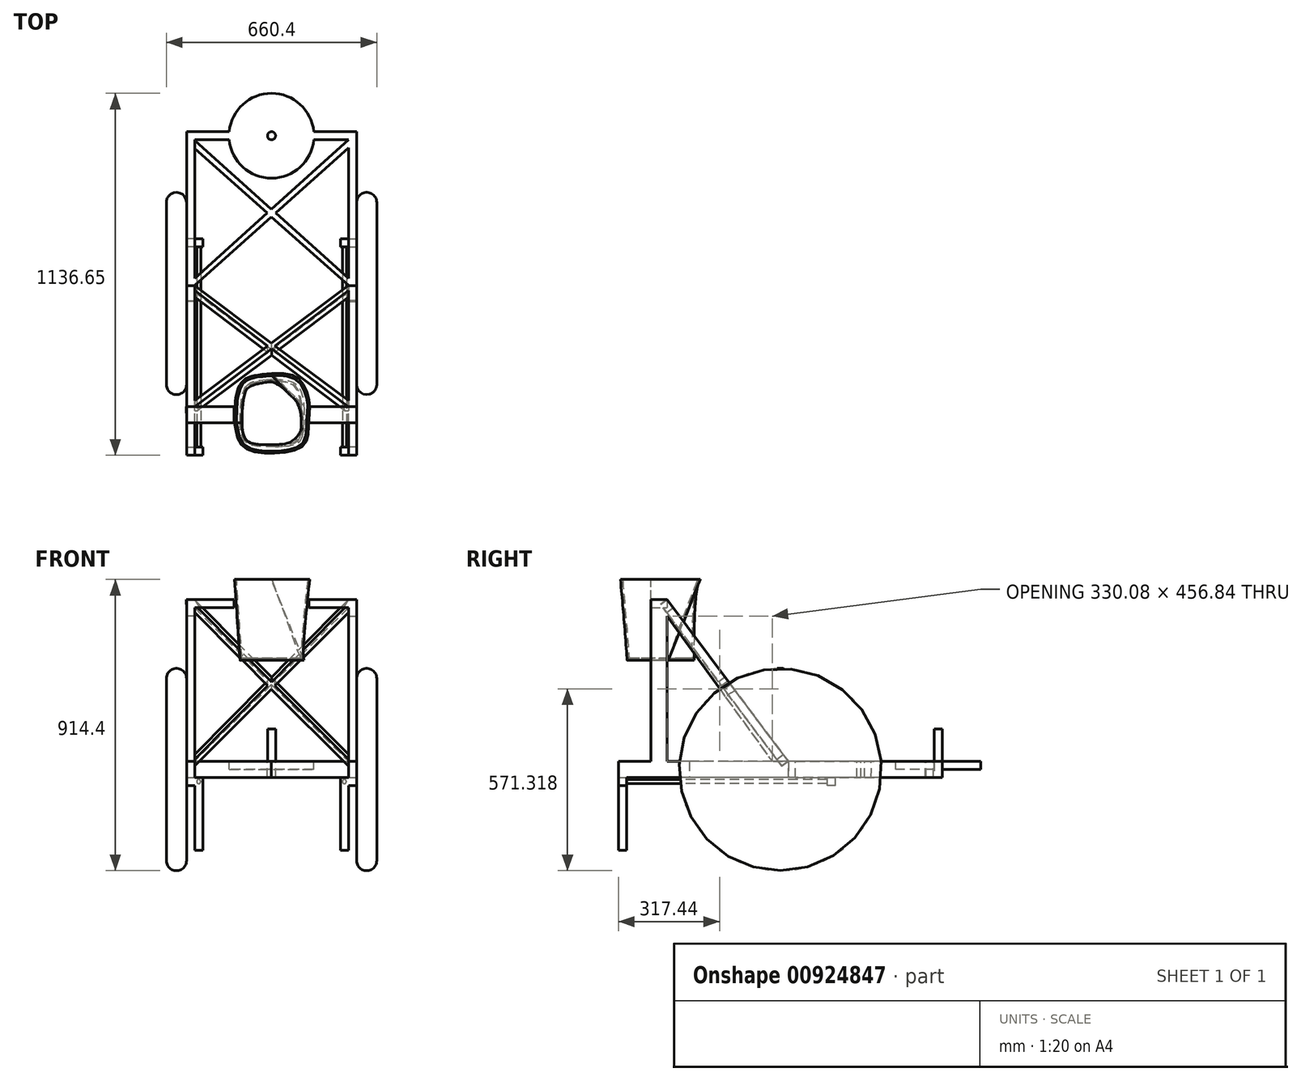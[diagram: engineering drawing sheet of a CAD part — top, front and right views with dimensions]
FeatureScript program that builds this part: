
annotation { "Feature Type Name" : "Feature", "Feature Type Description" : "" }
export const myFeature = defineFeature(function(context is Context, id is Id, definition is map)
    precondition{}
    {
        {
            var Q0;
            Q0=qCreatedBy(makeId("Right.planeOp"),FACE);
            var sketch = newSketch(context, id + "F0", { "sketchPlane" : qUnion([Q0])});
            skCircle(sketch, "E0", {"center": v(0, 317.5) * mm, "radius": 317.5 * mm});
            skSolve(sketch);
        }
        {
            var Q0;
            Q0=makeQuery(id+"F0.imprint","IMPRINT",FACE,{"disambiguationData":[TD([[makeQuery(id+"F0.imprint","IMPRINT",EDGE,{"derivedFrom":sQuery(id+"F0.wireOp",EDGE,"E0")}),1.0]])]});
            extrude(context, id + "F1", {"entities" : qUnion([Q0]), "depth" : 330.2 * mm, "offsetDistance" : 25.4 * mm, "hasSecondDirection" : true, "secondDirectionOppositeDirection" : false, "secondDirectionDepth" : 266.7 * mm});
        }
        {
            var Q0;
            Q0=makeQuery(id+"FX83OG7cxAnBelo_1.opExtrude","CAP_EDGE",EDGE,{"disambiguationData":[OSD([sQuery(id+"F0.wireOp",EDGE,"E0")])],"isStart":false});
            var Q1;
            Q1=makeQuery(id+"FX83OG7cxAnBelo_1.opExtrude","CAP_EDGE",EDGE,{"disambiguationData":[OSD([sQuery(id+"F0.wireOp",EDGE,"E0")])],"isStart":true});
            var Q2;
            Q2=makeQuery(id+"F1.opExtrude","CAP_EDGE",EDGE,{"disambiguationData":[OSD([sQuery(id+"F0.wireOp",EDGE,"E0")])],"isStart":true});
            var Q3;
            Q3=makeQuery(id+"F1.opExtrude","SWEPT_FACE",FACE,{"disambiguationData":[OSD([sQuery(id+"F0.wireOp",EDGE,"E0")])]});
            fillet(context, id + "F2", {"entities" : qUnion([Q0, Q1, Q2, Q3]), "radius" : 31.75 * mm, "tangentPropagation" : true, "allowEdgeOverflow" : false});
        }
        {
            var Q0;
            Q0=qCreatedBy(makeId("Top.planeOp"),FACE);
            cPlane(context, id + "F3", {"entities" : qUnion([Q0]), "cplaneType" : CPlaneType.OFFSET, "offset" : 317.5 * mm, "width" : 152.4 * mm, "height" : 152.4 * mm});
        }
        {
            var Q0;
            Q0=qCreatedBy(id+"F3.planeOp",FACE);
            var sketch = newSketch(context, id + "F4", { "sketchPlane" : qUnion([Q0])});
            skLineSegment(sketch, "E1.bottom", {"start": v(266.7, 508) * mm, "end": v(241.3, 508) * mm});
            skLineSegment(sketch, "E1.top", {"start": v(266.7, -508) * mm, "end": v(241.3, -508) * mm});
            skLineSegment(sketch, "E1.left", {"start": v(266.7, 508) * mm, "end": v(266.7, -508) * mm});
            skLineSegment(sketch, "E1.right", {"start": v(241.3, 508) * mm, "end": v(241.3, -508) * mm});
            skSolve(sketch);
        }
        {
            var Q0;
            Q0=makeQuery(id+"F4.imprint","IMPRINT",FACE,{"disambiguationData":[TD([[makeQuery(id+"F4.imprint","IMPRINT",EDGE,{"derivedFrom":sQuery(id+"F4.wireOp",EDGE,"E1.bottom")}),1.0]])]});
            extrude(context, id + "F5", {"entities" : qUnion([Q0]), "operationType" : NewBodyOperationType.ADD, "depth" : 25.4 * mm, "offsetDistance" : 25.4 * mm, "hasSecondDirection" : true, "secondDirectionOppositeDirection" : true, "secondDirectionDepth" : 25.4 * mm});
        }
        {
            var Q0;
            Q0=makeQuery(id+"F5.opExtrude","CAP_FACE",FACE,{"disambiguationData":[OSD([sQuery(id+"F4.wireOp",EDGE,"E1.bottom"),sQuery(id+"F4.wireOp",EDGE,"E1.top"),sQuery(id+"F4.wireOp",EDGE,"E1.left"),sQuery(id+"F4.wireOp",EDGE,"E1.right")])],"isStart":false});
            var sketch = newSketch(context, id + "F6", { "sketchPlane" : qUnion([Q0])});
            skLineSegment(sketch, "E2.bottom", {"start": v(266.7, -406.4) * mm, "end": v(241.3, -406.4) * mm});
            skLineSegment(sketch, "E2.top", {"start": v(266.7, -355.6) * mm, "end": v(241.3, -355.6) * mm});
            skLineSegment(sketch, "E2.left", {"start": v(266.7, -406.4) * mm, "end": v(266.7, -355.6) * mm});
            skLineSegment(sketch, "E2.right", {"start": v(241.3, -406.4) * mm, "end": v(241.3, -355.6) * mm});
            skSolve(sketch);
        }
        {
            var Q0;
            Q0=qSketchRegion(id+"F6",true);
            extrude(context, id + "F7", {"entities" : qUnion([Q0]), "operationType" : NewBodyOperationType.ADD, "depth" : 508 * mm, "offsetDistance" : 25.4 * mm});
        }
        {
            var Q0;
            Q0=makeQuery(id+"F5.opExtrude","CAP_FACE",FACE,{"disambiguationData":[OSD([sQuery(id+"F4.wireOp",EDGE,"E1.bottom"),sQuery(id+"F4.wireOp",EDGE,"E1.top"),sQuery(id+"F4.wireOp",EDGE,"E1.left"),sQuery(id+"F4.wireOp",EDGE,"E1.right")])],"isStart":true});
            var sketch = newSketch(context, id + "F8", { "sketchPlane" : qUnion([Q0])});
            skLineSegment(sketch, "E3.bottom", {"start": v(266.7, 508) * mm, "end": v(241.3, 508) * mm});
            skLineSegment(sketch, "E3.top", {"start": v(266.7, 482.6) * mm, "end": v(241.3, 482.6) * mm});
            skLineSegment(sketch, "E3.left", {"start": v(266.7, 508) * mm, "end": v(266.7, 482.6) * mm});
            skLineSegment(sketch, "E3.right", {"start": v(241.3, 508) * mm, "end": v(241.3, 482.6) * mm});
            skLineSegment(sketch, "E4.bottom", {"start": v(241.3, -172.43) * mm, "end": v(266.7, -172.43) * mm});
            skLineSegment(sketch, "E4.top", {"start": v(241.3, -147.03) * mm, "end": v(266.7, -147.03) * mm});
            skLineSegment(sketch, "E4.left", {"start": v(241.3, -172.43) * mm, "end": v(241.3, -147.03) * mm});
            skLineSegment(sketch, "E4.right", {"start": v(266.7, -172.43) * mm, "end": v(266.7, -147.03) * mm});
            skSolve(sketch);
        }
        {
            var Q0;
            Q0=qSketchRegion(id+"F8",true);
            extrude(context, id + "F9", {"entities" : qUnion([Q0]), "operationType" : NewBodyOperationType.ADD, "depth" : 25.4 * mm, "offsetDistance" : 25.4 * mm});
        }
        {
            var Q0;
            Q0=makeQuery(id+"F9.boolean.opBoolean","MERGE",FACE,{"derivedFrom":[makeQuery(id+"F7.boolean.opBoolean","MERGE",FACE,{"derivedFrom":[makeQuery(id+"F5.opExtrude","SWEPT_FACE",FACE,{"disambiguationData":[OSD([sQuery(id+"F4.wireOp",EDGE,"E1.right")])]}),makeQuery(id+"F7.opExtrude","SWEPT_FACE",FACE,{"disambiguationData":[OSD([sQuery(id+"F6.wireOp",EDGE,"E2.right")])]})]}),makeQuery(id+"F9.opExtrude","SWEPT_FACE",FACE,{"disambiguationData":[OSD([sQuery(id+"F8.wireOp",EDGE,"E3.right")])]}),makeQuery(id+"F9.opExtrude","SWEPT_FACE",FACE,{"disambiguationData":[OSD([sQuery(id+"F8.wireOp",EDGE,"2GlEI7fU-vQDi-rjw4-ohAJ-rqm9R4m0vmAV.right")])]})]});
            var sketch = newSketch(context, id + "F10", { "sketchPlane" : qUnion([Q0])});
            skLineSegment(sketch, "E5.bottom", {"start": v(508, 266.7) * mm, "end": v(482.6, 266.7) * mm});
            skLineSegment(sketch, "E5.top", {"start": v(508, 292.1) * mm, "end": v(482.6, 292.1) * mm});
            skLineSegment(sketch, "E5.left", {"start": v(508, 266.7) * mm, "end": v(508, 292.1) * mm});
            skLineSegment(sketch, "E5.right", {"start": v(482.6, 266.7) * mm, "end": v(482.6, 292.1) * mm});
            skLineSegment(sketch, "E6.bottom", {"start": v(-172.43, 266.7) * mm, "end": v(-147.03, 266.7) * mm});
            skLineSegment(sketch, "E6.top", {"start": v(-172.43, 292.1) * mm, "end": v(-147.03, 292.1) * mm});
            skLineSegment(sketch, "E6.left", {"start": v(-172.43, 266.7) * mm, "end": v(-172.43, 292.1) * mm});
            skLineSegment(sketch, "E6.right", {"start": v(-147.03, 266.7) * mm, "end": v(-147.03, 292.1) * mm});
            skSolve(sketch);
        }
        {
            var Q0;
            Q0=qSketchRegion(id+"F10",true);
            extrude(context, id + "F11", {"entities" : qUnion([Q0]), "operationType" : NewBodyOperationType.ADD, "depth" : 25.4 * mm, "offsetDistance" : 25.4 * mm});
        }
        {
            var Q0;
            Q0=makeQuery(id+"F11.boolean.opBoolean","MERGE",FACE,{"derivedFrom":[makeQuery(id+"F9.opExtrude","SWEPT_FACE",FACE,{"disambiguationData":[OSD([sQuery(id+"F8.wireOp",EDGE,"E3.top")])]}),makeQuery(id+"F11.opExtrude","SWEPT_FACE",FACE,{"disambiguationData":[OSD([sQuery(id+"F10.wireOp",EDGE,"E5.right")])]})]});
            var sketch = newSketch(context, id + "F12", { "sketchPlane" : qUnion([Q0])});
            skCircle(sketch, "E7", {"center": v(-228.6, 279.75) * mm, "radius": 6.35 * mm});
            skSolve(sketch);
        }
        {
            var Q0;
            Q0=qSketchRegion(id+"F12",true);
            extrude(context, id + "F13", {"entities" : qUnion([Q0]), "operationType" : NewBodyOperationType.ADD, "depth" : 635 * mm, "offsetDistance" : 25.4 * mm});
        }
        {
            var Q0;
            Q0=makeQuery(id+"F9.boolean.opBoolean","MERGE",FACE,{"derivedFrom":[makeQuery(id+"F7.boolean.opBoolean","MERGE",FACE,{"derivedFrom":[makeQuery(id+"F5.opExtrude","SWEPT_FACE",FACE,{"disambiguationData":[OSD([sQuery(id+"F4.wireOp",EDGE,"E1.right")])]}),makeQuery(id+"F7.opExtrude","SWEPT_FACE",FACE,{"disambiguationData":[OSD([sQuery(id+"F6.wireOp",EDGE,"E2.right")])]})]}),makeQuery(id+"F9.opExtrude","SWEPT_FACE",FACE,{"disambiguationData":[OSD([sQuery(id+"F8.wireOp",EDGE,"E3.right")])]}),makeQuery(id+"F9.opExtrude","SWEPT_FACE",FACE,{"disambiguationData":[OSD([sQuery(id+"F8.wireOp",EDGE,"2GlEI7fU-vQDi-rjw4-ohAJ-rqm9R4m0vmAV.right")])]})]});
            var sketch = newSketch(context, id + "F14", { "sketchPlane" : qUnion([Q0])});
            skLineSegment(sketch, "E8.bottom", {"start": v(406.4, 850.9) * mm, "end": v(355.6, 850.9) * mm});
            skLineSegment(sketch, "E8.top", {"start": v(406.4, 825.5) * mm, "end": v(355.6, 825.5) * mm});
            skLineSegment(sketch, "E8.left", {"start": v(406.4, 850.9) * mm, "end": v(406.4, 825.5) * mm});
            skLineSegment(sketch, "E8.right", {"start": v(355.6, 850.9) * mm, "end": v(355.6, 825.5) * mm});
            skSolve(sketch);
        }
        {
            var Q0;
            Q0=qSketchRegion(id+"F14",true);
            extrude(context, id + "F15", {"entities" : qUnion([Q0]), "operationType" : NewBodyOperationType.ADD, "depth" : 124.28 * mm, "offsetDistance" : 25.4 * mm});
        }
        {
            var Q0;
            {var subQ0=sQuery(id+"F0.wireOp",EDGE,"E0");var subQ1=sQuery(id+"F4.wireOp",EDGE,"E1.left");Q0=makeQuery(id+"F5.boolean.opBoolean","SPLIT",FACE,{"disambiguationData":[TD([makeQuery(id+"F5.opExtrude","CAP_FACE",FACE,{"disambiguationData":[OSD([sQuery(id+"F4.wireOp",EDGE,"E1.bottom"),sQuery(id+"F4.wireOp",EDGE,"E1.top"),subQ1,sQuery(id+"F4.wireOp",EDGE,"E1.right")])],"isStart":false})])],"derivedFrom":makeQuery(id+"F1.opExtrude","CAP_FACE",FACE,{"disambiguationData":[OSD([subQ0])],"isStart":true})});}
            cPlane(context, id + "F16", {"entities" : qUnion([Q0]), "cplaneType" : CPlaneType.OFFSET, "offset" : 0 * mm, "width" : 152.4 * mm, "height" : 152.4 * mm});
        }
        {
            var Q0;
            Q0=qCreatedBy(id+"F16.planeOp",FACE);
            var sketch = newSketch(context, id + "F17", { "sketchPlane" : qUnion([Q0])});
            skLineSegment(sketch, "E9", {"start": v(-24.25, 344.15) * mm, "end": v(355.63, 851.05) * mm});
            skLineSegment(sketch, "E10", {"start": v(355.63, 851.05) * mm, "end": v(355.63, 799.78) * mm});
            skLineSegment(sketch, "E11", {"start": v(355.63, 799.78) * mm, "end": v(25.47, 342.83) * mm});
            skLineSegment(sketch, "E12", {"start": v(25.47, 342.83) * mm, "end": v(-24.25, 344.15) * mm});
            skSolve(sketch);
        }
        {
            var Q0;
            Q0=qSketchRegion(id+"F17",true);
            extrude(context, id + "F18", {"entities" : qUnion([Q0]), "operationType" : NewBodyOperationType.ADD, "depth" : 25.4 * mm, "offsetDistance" : 25.4 * mm});
        }
        {
            var Q0;
            Q0=makeQuery(id+"F1.opExtrude","SWEPT_BODY",BODY,{"disambiguationData":[OSD([sQuery(id+"F0.wireOp",EDGE,"E0")])]});
            var Q1;
            Q1=qCreatedBy(makeId("Right.planeOp"),FACE);
            mirror(context, id + "F19", {"operationType" : NewBodyOperationType.ADD, "entities" : qUnion([Q0]), "mirrorPlane" : qUnion([Q1])});
        }
        {
            var Q0;
            Q0=makeQuery(id+"F18.opExtrude","SWEPT_FACE",FACE,{"disambiguationData":[OSD([sQuery(id+"F17.wireOp",EDGE,"E9")])]});
            cPlane(context, id + "F20", {"entities" : qUnion([Q0]), "cplaneType" : CPlaneType.OFFSET, "offset" : 0 * mm, "oppositeDirection" : true, "width" : 152.4 * mm, "height" : 152.4 * mm});
        }
        {
            var Q0;
            Q0=qCreatedBy(id+"F20.planeOp",FACE);
            var sketch = newSketch(context, id + "F21", { "sketchPlane" : qUnion([Q0])});
            skLineSegment(sketch, "E13", {"start": v(-266.64, 894.26) * mm, "end": v(241.25, 260.94) * mm});
            skLineSegment(sketch, "E14", {"start": v(241.25, 260.94) * mm, "end": v(241.25, 286.34) * mm});
            skLineSegment(sketch, "E15", {"start": v(241.25, 286.34) * mm, "end": v(-241.24, 894.26) * mm});
            skLineSegment(sketch, "E16", {"start": v(-241.24, 894.26) * mm, "end": v(-266.64, 894.26) * mm});
            skSolve(sketch);
        }
        {
            var Q0;
            Q0=qSketchRegion(id+"F21",true);
            extrude(context, id + "F22", {"entities" : qUnion([Q0]), "operationType" : NewBodyOperationType.ADD, "oppositeDirection" : true, "depth" : 25.4 * mm, "offsetDistance" : 25.4 * mm});
        }
        {
            var Q0;
            Q0=qCreatedBy(id+"F20.planeOp",FACE);
            var sketch = newSketch(context, id + "F23", { "sketchPlane" : qUnion([Q0])});
            skLineSegment(sketch, "E17", {"start": v(266.86, 894.36) * mm, "end": v(-241.47, 258.94) * mm});
            skLineSegment(sketch, "E18", {"start": v(-241.47, 258.94) * mm, "end": v(-241.47, 286.28) * mm});
            skLineSegment(sketch, "E19", {"start": v(-241.47, 286.28) * mm, "end": v(241.46, 893.97) * mm});
            skLineSegment(sketch, "E20", {"start": v(241.46, 893.97) * mm, "end": v(266.86, 894.36) * mm});
            skSolve(sketch);
        }
        {
            var Q0;
            Q0=qSketchRegion(id+"F23",true);
            extrude(context, id + "F24", {"entities" : qUnion([Q0]), "operationType" : NewBodyOperationType.ADD, "oppositeDirection" : true, "depth" : 25.4 * mm, "offsetDistance" : 25.4 * mm});
        }
        {
            var Q0;
            {var subQ0=sQuery(id+"F17.wireOp",EDGE,"E11");var subQ1=sQuery(id+"F17.wireOp",EDGE,"E9");var subQ6=sQuery(id+"F4.wireOp",EDGE,"E1.right");var subQ9=sQuery(id+"F4.wireOp",EDGE,"E1.bottom");var subQ10=sQuery(id+"F17.wireOp",EDGE,"E12");Q0=makeQuery(id+"F22.boolean.opBoolean","SPLIT",FACE,{"disambiguationData":[TD([makeQuery(id+"F5.opExtrude","SWEPT_FACE",FACE,{"disambiguationData":[OSD([subQ9])]})])],"derivedFrom":makeQuery(id+"F18.boolean.opBoolean","MERGE",FACE,{"derivedFrom":[makeQuery(id+"F9.boolean.opBoolean","MERGE",FACE,{"derivedFrom":[makeQuery(id+"F7.boolean.opBoolean","MERGE",FACE,{"derivedFrom":[makeQuery(id+"F5.opExtrude","SWEPT_FACE",FACE,{"disambiguationData":[OSD([subQ6])]}),makeQuery(id+"F7.opExtrude","SWEPT_FACE",FACE,{"disambiguationData":[OSD([sQuery(id+"F6.wireOp",EDGE,"E2.right")])]})]}),makeQuery(id+"F9.opExtrude","SWEPT_FACE",FACE,{"disambiguationData":[OSD([sQuery(id+"F8.wireOp",EDGE,"E3.right")])]}),makeQuery(id+"F9.opExtrude","SWEPT_FACE",FACE,{"disambiguationData":[OSD([sQuery(id+"F8.wireOp",EDGE,"E4.left")])]})]}),makeQuery(id+"F18.opExtrude","CAP_FACE",FACE,{"disambiguationData":[OSD([subQ1,sQuery(id+"F17.wireOp",EDGE,"E10"),subQ0,subQ10])],"isStart":false})]})});}
            var sketch = newSketch(context, id + "F25", { "sketchPlane" : qUnion([Q0])});
            skLineSegment(sketch, "E21.bottom", {"start": v(-508, 342.9) * mm, "end": v(-482.6, 342.9) * mm});
            skLineSegment(sketch, "E21.top", {"start": v(-508, 292.1) * mm, "end": v(-482.6, 292.1) * mm});
            skLineSegment(sketch, "E21.left", {"start": v(-508, 342.9) * mm, "end": v(-508, 292.1) * mm});
            skLineSegment(sketch, "E21.right", {"start": v(-482.6, 342.9) * mm, "end": v(-482.6, 292.1) * mm});
            skSolve(sketch);
        }
        {
            var Q0;
            Q0=qSketchRegion(id+"F25",true);
            extrude(context, id + "F26", {"entities" : qUnion([Q0]), "operationType" : NewBodyOperationType.ADD, "depth" : 482.6 * mm, "offsetDistance" : 25.4 * mm});
        }
        {
            var Q0;
            {var subQ0=sQuery(id+"F4.wireOp",EDGE,"E1.left");var subQ2=sQuery(id+"F4.wireOp",EDGE,"E1.bottom");var subQ3=makeQuery(id+"F5.opExtrude","SWEPT_FACE",FACE,{"disambiguationData":[OSD([subQ2])]});var subQ4=sQuery(id+"F0.wireOp",EDGE,"E0");var subQ6=makeQuery(id+"F1.opExtrude","CAP_FACE",FACE,{"disambiguationData":[OSD([subQ4])],"isStart":true});var subQ8=sQuery(id+"F4.wireOp",EDGE,"E1.right");var subQ11=makeQuery(id+"F18.boolean.opBoolean","SPLIT",FACE,{"disambiguationData":[TD([subQ3])],"derivedFrom":makeQuery(id+"F7.boolean.opBoolean","SPLIT",FACE,{"disambiguationData":[TD([subQ6])],"derivedFrom":makeQuery(id+"F5.opExtrude","CAP_FACE",FACE,{"disambiguationData":[OSD([subQ2,sQuery(id+"F4.wireOp",EDGE,"E1.top"),subQ0,subQ8])],"isStart":false})})});Q0=makeQuery(id+"F26.boolean.opBoolean","MERGE",FACE,{"derivedFrom":[makeQuery(id+"F19.opPattern","COPY",FACE,{"derivedFrom":subQ11,"instanceName":"1"}),subQ11,makeQuery(id+"F26.opExtrude","SWEPT_FACE",FACE,{"disambiguationData":[OSD([sQuery(id+"F25.wireOp",EDGE,"E21.bottom")])]})]});}
            var sketch = newSketch(context, id + "F27", { "sketchPlane" : qUnion([Q0])});
            skCircle(sketch, "E22", {"center": v(0, 495.3) * mm, "radius": 133.35 * mm});
            skPoint(sketch, "E22.centerSnap0", {"position": v(0, 482.6) * mm});
            skSolve(sketch);
        }
        {
            var Q0;
            {var subQ0=sQuery(id+"F27.wireOp",EDGE,"E22");var subQ1=makeQuery(id+"F26.opExtrude","SWEPT_EDGE",EDGE,{"disambiguationData":[OSD([sQuery(id+"F4.wireOp",EDGE,"E1.right"),sQuery(id+"F25.wireOp",EDGE,"E21.bottom"),sQuery(id+"F25.wireOp",EDGE,"E21.right")])]});var subQ2=makeQuery(id+"F27.imprint","INTERSECT",VERTEX,{"disambiguationData":[OD(0.0)],"derivedFrom":[subQ1,subQ0]});Q0=makeQuery(id+"F27.imprint","IMPRINT",FACE,{"disambiguationData":[TD([[makeQuery(id+"F27.imprint","IMPRINT",EDGE,{"disambiguationData":[TD([[subQ2,-1.0]])],"derivedFrom":subQ0}),1.0]])]});}
            var Q1;
            {var subQ0=sQuery(id+"F27.wireOp",EDGE,"E22");var subQ1=sQuery(id+"F25.wireOp",EDGE,"E21.bottom");var subQ5=makeQuery(id+"F26.opExtrude","SWEPT_EDGE",EDGE,{"disambiguationData":[OSD([sQuery(id+"F4.wireOp",EDGE,"E1.right"),subQ1,sQuery(id+"F25.wireOp",EDGE,"E21.right")])]});var subQ6=makeQuery(id+"F27.imprint","INTERSECT",VERTEX,{"disambiguationData":[OD(0.0)],"derivedFrom":[subQ5,subQ0]});Q1=makeQuery(id+"F27.imprint","IMPRINT",FACE,{"disambiguationData":[TD([[makeQuery(id+"F27.imprint","IMPRINT",EDGE,{"disambiguationData":[TD([[subQ6,1.0]])],"derivedFrom":subQ0}),1.0]])]});}
            var Q2;
            {var subQ0=sQuery(id+"F27.wireOp",EDGE,"E22");var subQ1=makeQuery(id+"F5.opExtrude","CAP_EDGE",EDGE,{"disambiguationData":[OSD([sQuery(id+"F4.wireOp",EDGE,"E1.bottom")])],"isStart":false});var subQ2=makeQuery(id+"F26.boolean.opBoolean","MERGE",EDGE,{"derivedFrom":[subQ1,makeQuery(id+"F19.opPattern","COPY",EDGE,{"derivedFrom":subQ1,"instanceName":"1"}),makeQuery(id+"F26.opExtrude","SWEPT_EDGE",EDGE,{"disambiguationData":[OSD([sQuery(id+"F25.wireOp",EDGE,"E21.bottom"),sQuery(id+"F25.wireOp",EDGE,"E21.left")])]})]});var subQ3=makeQuery(id+"F27.imprint","INTERSECT",VERTEX,{"disambiguationData":[OD(0.0)],"derivedFrom":[subQ2,subQ0]});Q2=makeQuery(id+"F27.imprint","IMPRINT",FACE,{"disambiguationData":[TD([[makeQuery(id+"F27.imprint","IMPRINT",EDGE,{"disambiguationData":[TD([[subQ3,1.0]])],"derivedFrom":subQ0}),1.0]])]});}
            extrude(context, id + "F28", {"entities" : qUnion([Q0, Q1, Q2]), "operationType" : NewBodyOperationType.ADD, "oppositeDirection" : true, "depth" : 25.4 * mm, "offsetDistance" : 25.4 * mm});
        }
        {
            var Q0;
            {var subQ0=sQuery(id+"F4.wireOp",EDGE,"E1.left");var subQ2=sQuery(id+"F4.wireOp",EDGE,"E1.bottom");var subQ3=makeQuery(id+"F5.opExtrude","SWEPT_FACE",FACE,{"disambiguationData":[OSD([subQ2])]});var subQ4=sQuery(id+"F0.wireOp",EDGE,"E0");var subQ6=makeQuery(id+"F1.opExtrude","CAP_FACE",FACE,{"disambiguationData":[OSD([subQ4])],"isStart":true});var subQ8=sQuery(id+"F4.wireOp",EDGE,"E1.right");var subQ11=makeQuery(id+"F18.boolean.opBoolean","SPLIT",FACE,{"disambiguationData":[TD([subQ3])],"derivedFrom":makeQuery(id+"F7.boolean.opBoolean","SPLIT",FACE,{"disambiguationData":[TD([subQ6])],"derivedFrom":makeQuery(id+"F5.opExtrude","CAP_FACE",FACE,{"disambiguationData":[OSD([subQ2,sQuery(id+"F4.wireOp",EDGE,"E1.top"),subQ0,subQ8])],"isStart":false})})});Q0=makeQuery(id+"F28.boolean.opBoolean","MERGE",FACE,{"derivedFrom":[makeQuery(id+"F26.boolean.opBoolean","MERGE",FACE,{"derivedFrom":[makeQuery(id+"F19.opPattern","COPY",FACE,{"derivedFrom":subQ11,"instanceName":"1"}),subQ11,makeQuery(id+"F26.opExtrude","SWEPT_FACE",FACE,{"disambiguationData":[OSD([sQuery(id+"F25.wireOp",EDGE,"E21.bottom")])]})]}),makeQuery(id+"F28.opExtrude","CAP_FACE",FACE,{"disambiguationData":[OSD([sQuery(id+"F27.wireOp",EDGE,"E22")])],"isStart":true})]});}
            var sketch = newSketch(context, id + "F29", { "sketchPlane" : qUnion([Q0])});
            skCircle(sketch, "E23", {"center": v(0, 495.3) * mm, "radius": 12.7 * mm});
            skSolve(sketch);
        }
        {
            var Q0;
            Q0=makeQuery(id+"F29.imprint","IMPRINT",FACE,{"disambiguationData":[TD([[makeQuery(id+"F29.imprint","IMPRINT",EDGE,{"derivedFrom":sQuery(id+"F29.wireOp",EDGE,"E23")}),1.0]])]});
            extrude(context, id + "F30", {"entities" : qUnion([Q0]), "operationType" : NewBodyOperationType.ADD, "depth" : 101.6 * mm, "offsetDistance" : 25.4 * mm});
        }
        {
            var Q0;
            {var subQ0=sQuery(id+"F4.wireOp",EDGE,"E1.left");var subQ2=sQuery(id+"F4.wireOp",EDGE,"E1.bottom");var subQ3=makeQuery(id+"F5.opExtrude","SWEPT_FACE",FACE,{"disambiguationData":[OSD([subQ2])]});var subQ4=sQuery(id+"F0.wireOp",EDGE,"E0");var subQ6=makeQuery(id+"F1.opExtrude","CAP_FACE",FACE,{"disambiguationData":[OSD([subQ4])],"isStart":true});var subQ8=sQuery(id+"F4.wireOp",EDGE,"E1.right");var subQ11=makeQuery(id+"F18.boolean.opBoolean","SPLIT",FACE,{"disambiguationData":[TD([subQ3])],"derivedFrom":makeQuery(id+"F7.boolean.opBoolean","SPLIT",FACE,{"disambiguationData":[TD([subQ6])],"derivedFrom":makeQuery(id+"F5.opExtrude","CAP_FACE",FACE,{"disambiguationData":[OSD([subQ2,sQuery(id+"F4.wireOp",EDGE,"E1.top"),subQ0,subQ8])],"isStart":false})})});Q0=makeQuery(id+"F28.boolean.opBoolean","MERGE",FACE,{"derivedFrom":[makeQuery(id+"F26.boolean.opBoolean","MERGE",FACE,{"derivedFrom":[makeQuery(id+"F19.opPattern","COPY",FACE,{"derivedFrom":subQ11,"instanceName":"1"}),subQ11,makeQuery(id+"F26.opExtrude","SWEPT_FACE",FACE,{"disambiguationData":[OSD([sQuery(id+"F25.wireOp",EDGE,"E21.bottom")])]})]}),makeQuery(id+"F28.opExtrude","CAP_FACE",FACE,{"disambiguationData":[OSD([sQuery(id+"F27.wireOp",EDGE,"E22")])],"isStart":true})]});}
            var sketch = newSketch(context, id + "F31", { "sketchPlane" : qUnion([Q0])});
            skLineSegment(sketch, "E24", {"start": v(-266.7, 24.65) * mm, "end": v(241.3, 482.6) * mm});
            skLineSegment(sketch, "E25", {"start": v(241.3, 482.6) * mm, "end": v(241.3, 457.2) * mm});
            skLineSegment(sketch, "E26", {"start": v(241.3, 457.2) * mm, "end": v(-241.3, 25.19) * mm});
            skLineSegment(sketch, "E27", {"start": v(-241.3, 25.19) * mm, "end": v(-266.7, 24.65) * mm});
            skLineSegment(sketch, "E28", {"start": v(266.7, 24.54) * mm, "end": v(-241.23, 480.61) * mm});
            skLineSegment(sketch, "E29", {"start": v(-241.23, 480.61) * mm, "end": v(-241.23, 455.21) * mm});
            skLineSegment(sketch, "E30", {"start": v(-241.23, 455.21) * mm, "end": v(241.47, 25.19) * mm});
            skLineSegment(sketch, "E31", {"start": v(241.3, 25.2) * mm, "end": v(266.7, 24.54) * mm});
            skSolve(sketch);
        }
        {
            var Q0;
            Q0=qSketchRegion(id+"F31",true);
            extrude(context, id + "F32", {"entities" : qUnion([Q0]), "operationType" : NewBodyOperationType.ADD, "oppositeDirection" : true, "depth" : 50.8 * mm, "offsetDistance" : 25.4 * mm});
        }
        {
            var Q0;
            Q0=makeQuery(id+"F19.opPattern","COPY",FACE,{"derivedFrom":makeQuery(id+"F11.boolean.opBoolean","MERGE",FACE,{"derivedFrom":[makeQuery(id+"F9.opExtrude","CAP_FACE",FACE,{"disambiguationData":[OSD([sQuery(id+"F8.wireOp",EDGE,"E3.bottom"),sQuery(id+"F8.wireOp",EDGE,"E3.top"),sQuery(id+"F8.wireOp",EDGE,"E3.left"),sQuery(id+"F8.wireOp",EDGE,"E3.right")])],"isStart":false}),makeQuery(id+"F11.opExtrude","SWEPT_FACE",FACE,{"disambiguationData":[OSD([sQuery(id+"F10.wireOp",EDGE,"E5.bottom")])]})]}),"instanceName":"1"});
            var sketch = newSketch(context, id + "F33", { "sketchPlane" : qUnion([Q0])});
            skLineSegment(sketch, "E32.bottom", {"start": v(-215.9, 508) * mm, "end": v(-241.3, 508) * mm});
            skLineSegment(sketch, "E32.top", {"start": v(-215.9, 482.6) * mm, "end": v(-241.3, 482.6) * mm});
            skLineSegment(sketch, "E32.left", {"start": v(-215.9, 508) * mm, "end": v(-215.9, 482.6) * mm});
            skLineSegment(sketch, "E32.right", {"start": v(-241.3, 508) * mm, "end": v(-241.3, 482.6) * mm});
            skSolve(sketch);
        }
        {
            var Q0;
            Q0=qSketchRegion(id+"F33",true);
            extrude(context, id + "F34", {"entities" : qUnion([Q0]), "operationType" : NewBodyOperationType.ADD, "depth" : 203.2 * mm, "offsetDistance" : 25.4 * mm});
        }
        {
            var Q0;
            Q0=makeQuery(id+"F11.boolean.opBoolean","MERGE",FACE,{"derivedFrom":[makeQuery(id+"F9.opExtrude","CAP_FACE",FACE,{"disambiguationData":[OSD([sQuery(id+"F8.wireOp",EDGE,"E3.bottom"),sQuery(id+"F8.wireOp",EDGE,"E3.top"),sQuery(id+"F8.wireOp",EDGE,"E3.left"),sQuery(id+"F8.wireOp",EDGE,"E3.right")])],"isStart":false}),makeQuery(id+"F11.opExtrude","SWEPT_FACE",FACE,{"disambiguationData":[OSD([sQuery(id+"F10.wireOp",EDGE,"E5.bottom")])]})]});
            var sketch = newSketch(context, id + "F35", { "sketchPlane" : qUnion([Q0])});
            skLineSegment(sketch, "E33.bottom", {"start": v(215.9, 508) * mm, "end": v(241.3, 508) * mm});
            skLineSegment(sketch, "E33.top", {"start": v(215.9, 482.6) * mm, "end": v(241.3, 482.6) * mm});
            skLineSegment(sketch, "E33.left", {"start": v(215.9, 508) * mm, "end": v(215.9, 482.6) * mm});
            skLineSegment(sketch, "E33.right", {"start": v(241.3, 508) * mm, "end": v(241.3, 482.6) * mm});
            skSolve(sketch);
        }
        {
            var Q0;
            Q0=qSketchRegion(id+"F35",true);
            extrude(context, id + "F36", {"entities" : qUnion([Q0]), "operationType" : NewBodyOperationType.ADD, "depth" : 203.2 * mm, "offsetDistance" : 25.4 * mm});
        }
        {
            var Q0;
            Q0=qCreatedBy(makeId("Top.planeOp"),FACE);
            cPlane(context, id + "F37", {"entities" : qUnion([Q0]), "cplaneType" : CPlaneType.OFFSET, "offset" : 914.4 * mm, "width" : 152.4 * mm, "height" : 152.4 * mm});
        }
        {
            var Q0;
            Q0=qCreatedBy(id+"F37.planeOp",FACE);
            var sketch = newSketch(context, id + "F38", { "sketchPlane" : qUnion([Q0])});
            skFitSpline(sketch, "E34", {"points": [v(-116.29, -406.52) * mm, v(-114.53, -353.7) * mm, v(-93.4, -278) * mm, v(0, -251.6) * mm], "startDerivative": vector(5.7, 179.42) * mm, "endDerivative": vector(346.1, 27.63) * mm});
            skFitSpline(sketch, "E35", {"points": [v(0, -251.6) * mm, v(94.97, -278) * mm, v(119.62, -353.7) * mm, v(116.1, -406.52) * mm, v(103.78, -473.42) * mm, v(0, -501.59) * mm, v(-93.4, -476.94) * mm, v(-116.29, -406.52) * mm], "startDerivative": vector(965.92, 66.74) * mm, "endDerivative": vector(-120.36, 547.83) * mm});
            skSolve(sketch);
        }
        {
            var Q0;
            Q0=qCreatedBy(makeId("Top.planeOp"),FACE);
            cPlane(context, id + "F39", {"entities" : qUnion([Q0]), "cplaneType" : CPlaneType.OFFSET, "offset" : 660.4 * mm, "width" : 152.4 * mm, "height" : 152.4 * mm});
        }
        {
            var Q0;
            Q0=qCreatedBy(id+"F39.planeOp",FACE);
            var sketch = newSketch(context, id + "F40", { "sketchPlane" : qUnion([Q0])});
            skFitSpline(sketch, "E36", {"points": [v(-98.8, -406.39) * mm, v(-96.6, -350.68) * mm, v(-75.64, -287.24) * mm, v(0, -270.14) * mm, v(76.6, -284.48) * mm, v(101.42, -353.43) * mm, v(98.11, -433.97) * mm, v(82.67, -470.37) * mm, v(0, -480.85) * mm, v(-82.26, -465.96) * mm, v(-98.8, -406.39) * mm]});
            skSolve(sketch);
        }
        {
            var Q0;
            Q0=makeQuery(id+"F40.imprint","IMPRINT",FACE,{"disambiguationData":[TD([[makeQuery(id+"F40.imprint","IMPRINT",EDGE,{"derivedFrom":sQuery(id+"F40.wireOp",EDGE,"E36")}),-1.0]])]});
            var Q1;
            Q1=makeQuery(id+"F38.imprint","IMPRINT",FACE,{"disambiguationData":[TD([[makeQuery(id+"F38.imprint","IMPRINT",EDGE,{"derivedFrom":sQuery(id+"F38.wireOp",EDGE,"E34")}),-1.0]])]});
            loft(context, id + "F41", {"sheetProfilesArray" : [{ "sheetProfileEntities" : qUnion([Q0]) }, { "sheetProfileEntities" : qUnion([Q1]) }]});
        }
        {
            var Q0;
            Q0=makeQuery(id+"F41.opLoft","CAP_FACE",FACE,{"disambiguationData":[OSD([makeQuery(id+"F38.imprint","IMPRINT",FACE,{"disambiguationData":[TD([[makeQuery(id+"F38.imprint","IMPRINT",EDGE,{"derivedFrom":sQuery(id+"F38.wireOp",EDGE,"E34")}),-1.0]])]})])],"isStart":true});
            shell(context, id + "F42", {"entities" : qUnion([Q0]), "thickness" : 6.35 * mm});
        }
        {
            var Q0;
            Q0=qCreatedBy(id+"F39.planeOp",FACE);
            var sketch = newSketch(context, id + "F43", { "sketchPlane" : qUnion([Q0])});
            skFitSpline(sketch, "E37.0", {"points": [v(94.97, -352.2) * mm, v(94.66, -348.12) * mm, v(93.85, -340) * mm, v(91.96, -328.27) * mm, v(89.27, -317.27) * mm, v(85.68, -307.32) * mm, v(81.88, -300.15) * mm, v(78.34, -295.2) * mm, v(75.91, -292.45) * mm, v(73.84, -290.46) * mm, v(72.21, -289.07) * mm, v(70.5, -287.78) * mm, v(68.1, -286.17) * mm, v(64.84, -284.35) * mm, v(59.15, -281.85) * mm, v(51.14, -279.47) * mm, v(40.31, -277.64) * mm, v(28.53, -276.67) * mm, v(18.14, -276.4) * mm, v(9.62, -276.39) * mm, v(3.13, -276.45) * mm, v(-3.4, -276.54) * mm, v(-9.88, -276.66) * mm, v(-16.28, -276.86) * mm, v(-24.68, -277.26) * mm, v(-34.79, -278.1) * mm, v(-46.03, -279.88) * mm, v(-54.4, -282.18) * mm, v(-60.35, -284.57) * mm, v(-64.41, -286.65) * mm, v(-67.45, -288.64) * mm, v(-69.68, -290.4) * mm, v(-71.24, -291.8) * mm, v(-72.72, -293.3) * mm, v(-74.6, -295.44) * mm, v(-76.75, -298.4) * mm, v(-79.07, -302.37) * mm, v(-81.82, -308.16) * mm, v(-84.6, -316.2) * mm, v(-86.65, -324.94) * mm, v(-87.93, -332.13) * mm, v(-88.73, -337.55) * mm, v(-89.4, -342.96) * mm, v(-89.99, -348.3) * mm, v(-90.5, -353.5) * mm, v(-90.96, -358.52) * mm, v(-91.37, -363.4) * mm, v(-91.83, -369.72) * mm, v(-92.27, -377.42) * mm, v(-92.57, -386.58) * mm, v(-92.65, -395.95) * mm, v(-92.55, -402.5) * mm, v(-92.47, -405.91) * mm]});
            skFitSpline(sketch, "E37.1", {"points": [v(-92.47, -405.91) * mm, v(-92.38, -409.32) * mm, v(-92.14, -416.32) * mm, v(-91.28, -426.96) * mm, v(-89.67, -437.25) * mm, v(-87.52, -445.13) * mm, v(-85.25, -450.77) * mm, v(-83.59, -453.98) * mm, v(-82.1, -456.33) * mm, v(-80.92, -457.99) * mm, v(-79.66, -459.53) * mm, v(-78.33, -460.96) * mm, v(-76.9, -462.28) * mm, v(-74.83, -463.94) * mm, v(-71.95, -465.82) * mm, v(-68, -467.78) * mm, v(-63.58, -469.46) * mm, v(-58.7, -470.85) * mm, v(-51.68, -472.35) * mm, v(-41.97, -473.61) * mm, v(-31.33, -474.22) * mm, v(-22.41, -474.44) * mm, v(-15.57, -474.51) * mm, v(-9.75, -474.52) * mm, v(-5.06, -474.51) * mm, v(-1.52, -474.5) * mm, v(2.03, -474.5) * mm, v(6.76, -474.5) * mm, v(12.65, -474.49) * mm, v(19.63, -474.45) * mm, v(28.78, -474.33) * mm, v(39.82, -473.97) * mm, v(52.06, -473.03) * mm, v(61.1, -471.67) * mm, v(67.45, -470.17) * mm, v(71, -469.07) * mm, v(73.55, -468.09) * mm, v(75.32, -467.3) * mm, v(76.95, -466.47) * mm, v(78.4, -465.6) * mm, v(79.72, -464.7) * mm, v(81.32, -463.41) * mm, v(83.05, -461.67) * mm, v(84.82, -459.3) * mm, v(86.34, -456.6) * mm, v(87.65, -453.51) * mm, v(88.77, -450.05) * mm, v(89.71, -446.23) * mm, v(90.52, -442.06) * mm, v(91.1, -438.32) * mm, v(91.55, -435.18) * mm, v(91.87, -432.76) * mm, v(92.19, -430.28) * mm, v(92.6, -426.92) * mm, v(93.1, -422.6) * mm, v(93.67, -417.27) * mm, v(94.36, -409.97) * mm, v(95.08, -400.5) * mm, v(95.67, -388.75) * mm, v(95.9, -376.7) * mm, v(95.72, -364.47) * mm, v(95.28, -356.29) * mm, v(94.97, -352.2) * mm]});
            skSolve(sketch);
        }
        {
            var Q0;
            Q0=makeQuery(id+"F43.imprint","IMPRINT",FACE,{"disambiguationData":[TD([[makeQuery(id+"F43.imprint","IMPRINT",EDGE,{"derivedFrom":sQuery(id+"F43.wireOp",EDGE,"E37.0")}),1.0]])]});
            extrude(context, id + "F44", {"entities" : qUnion([Q0]), "operationType" : NewBodyOperationType.REMOVE, "depth" : 6.35 * mm, "offsetDistance" : 25.4 * mm});
        }
    });
